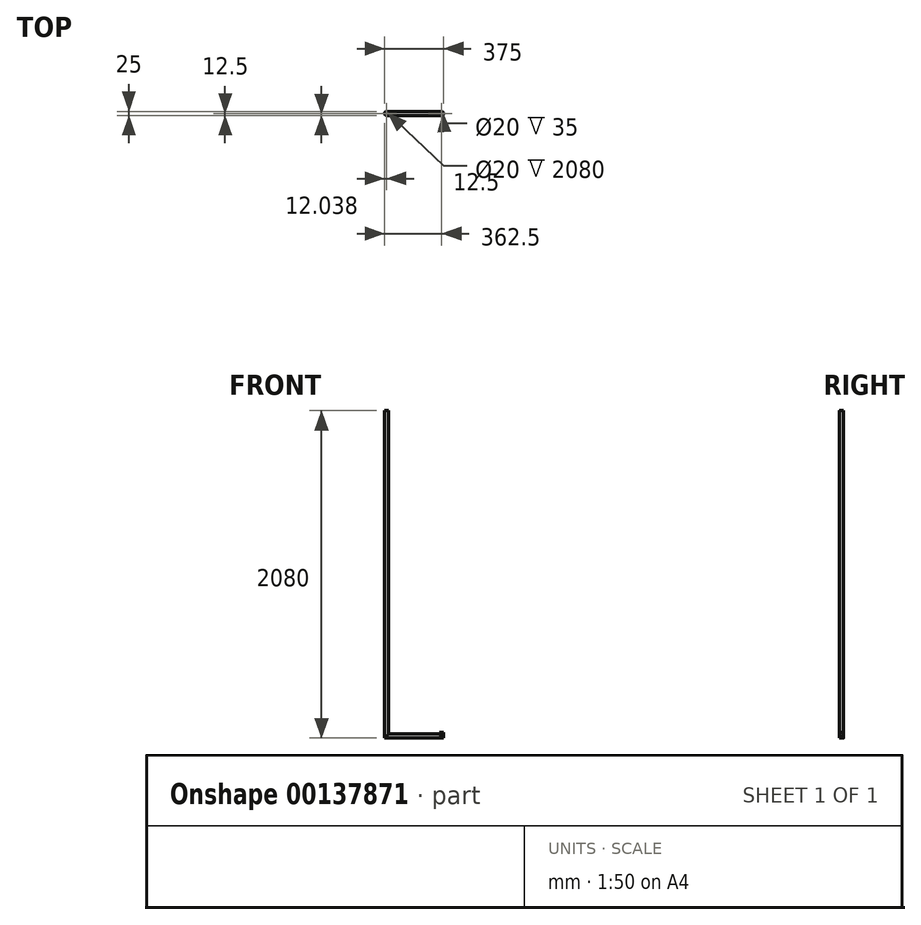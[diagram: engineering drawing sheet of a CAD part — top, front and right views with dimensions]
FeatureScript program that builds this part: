
annotation { "Feature Type Name" : "Feature", "Feature Type Description" : "" }
export const myFeature = defineFeature(function(context is Context, id is Id, definition is map)
    precondition{}
    {
        {
            var Q0;
            Q0=qCreatedBy(makeId("Top.planeOp"),FACE);
            var sketch = newSketch(context, id + "F0", { "sketchPlane" : qUnion([Q0])});
            skCircle(sketch, "E0", {"center": v(0, 0) * mm, "radius": 12.5 * mm});
            skCircle(sketch, "E1", {"center": v(350, 0) * mm, "radius": 12.5 * mm});
            skSolve(sketch);
        }
        {
            var Q0;
            Q0=makeQuery(id+"F0.imprint","IMPRINT",FACE,{"disambiguationData":[TD([[makeQuery(id+"F0.imprint","IMPRINT",EDGE,{"derivedFrom":sQuery(id+"F0.wireOp",EDGE,"E0")}),1.0]])]});
            extrude(context, id + "F1", {"entities" : qUnion([Q0]), "depth" : 1040 * mm});
        }
        {
            var Q0;
            Q0=makeQuery(id+"F0.imprint","IMPRINT",FACE,{"disambiguationData":[TD([[makeQuery(id+"F0.imprint","IMPRINT",EDGE,{"derivedFrom":sQuery(id+"F0.wireOp",EDGE,"E1")}),1.0]])]});
            extrude(context, id + "F2", {"entities" : qUnion([Q0]), "operationType" : NewBodyOperationType.ADD, "depth" : 35 * mm});
        }
        {
            var Q0;
            Q0=qCreatedBy(makeId("Right.planeOp"),FACE);
            var sketch = newSketch(context, id + "F3", { "sketchPlane" : qUnion([Q0])});
            skCircle(sketch, "E2", {"center": v(0, 12.5) * mm, "radius": 12.5 * mm});
            skLineSegment(sketch, "E3", {"start": v(-12.5, 0) * mm, "end": v(-12.5, 1040) * mm});
            skLineSegment(sketch, "E4", {"start": v(12.5, 1040) * mm, "end": v(12.5, 0) * mm});
            skLineSegment(sketch, "E5", {"start": v(12.5, 1040) * mm, "end": v(12.5, 0) * mm, "construction": true});
            skLineSegment(sketch, "E6", {"start": v(-12.5, 0) * mm, "end": v(-12.5, 1040) * mm, "construction": true});
            skSolve(sketch);
        }
        {
            var Q0;
            Q0=qSketchRegion(id+"F3",true);
            var Q1;
            Q1=sQuery(id+"F3.wireOp",EDGE,"E2");
            var Q2;
            Q2=makeQuery(id+"F2.opExtrude","SWEPT_BODY",BODY,{"disambiguationData":[OSD([sQuery(id+"F0.wireOp",EDGE,"E1")])]});
            extrude(context, id + "F4", {"entities" : qUnion([Q0]), "surfaceEntities" : qUnion([Q1]), "endBound" : BoundingType.UP_TO_BODY, "endBoundEntityBody" : qUnion([Q2]), "depth" : 25 * mm});
        }
        {
            var Q0;
            Q0=makeQuery(id+"F1.opExtrude","CAP_FACE",FACE,{"disambiguationData":[OSD([sQuery(id+"F0.wireOp",EDGE,"E0")])],"isStart":false});
            var sketch = newSketch(context, id + "F5", { "sketchPlane" : qUnion([Q0])});
            skCircle(sketch, "E7", {"center": v(0, 0) * mm, "radius": 10 * mm});
            skCircle(sketch, "E8", {"center": v(350, -0.46) * mm, "radius": 10 * mm});
            skSolve(sketch);
        }
        {
            var Q0;
            Q0=qSketchRegion(id+"F5",true);
            extrude(context, id + "F6", {"entities" : qUnion([Q0]), "operationType" : NewBodyOperationType.REMOVE, "endBound" : BoundingType.THROUGH_ALL, "oppositeDirection" : true, "depth" : 25 * mm});
        }
        {
            var Q0;
            Q0=makeQuery(id+"F1.opExtrude","SWEPT_BODY",BODY,{"disambiguationData":[OSD([sQuery(id+"F0.wireOp",EDGE,"E0")])]});
            var Q1;
            Q1=makeQuery(id+"F1.opExtrude","CAP_FACE",FACE,{"disambiguationData":[OSD([sQuery(id+"F0.wireOp",EDGE,"E0")])],"isStart":false});
            mirror(context, id + "F7", {"operationType" : NewBodyOperationType.ADD, "entities" : qUnion([Q0]), "mirrorPlane" : qUnion([Q1])});
        }
    });
